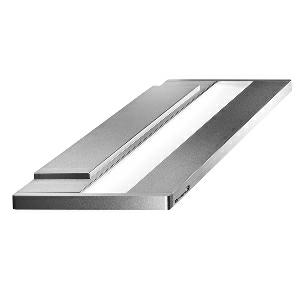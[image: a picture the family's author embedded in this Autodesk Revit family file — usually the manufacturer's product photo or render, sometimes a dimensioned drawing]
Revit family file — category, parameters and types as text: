
# Revit family: zera_bed_-_zew_11000_830_-_ul_nl_00813006_8f84
name_source: partatom
category: Lighting Fixtures
units: mm (PartAtom-declared; Revit-internal decimal feet)

## family parameters
Cut with Voids When Loaded = No
Host = Face
Light Source = No
Part Type = Normal
Room Calculation Point = No
Round Connector Dimension = Use Diameter
Shared = No

## types (1)
- AL+UL (1 x LED, 9800 lm, 4000K/3000K)
    Apparent Load = 109 VA
    Approval mark = CE
    CIE Flux Codes = 45 81 99 47 100
    Color Rendering = 90/80
    Color Temperature = 4000K/3000K
    Default Elevation = 2000 mm  [stored 6.56168 ft]
    Description = ZEW 11000/830|Wall-mounted luminaire|light source:   Warm white   |work equipment: Power supply unit|luminous flux: 10890 lm|light distribution: Direct/indirect|class of protection: I|technology: Switchable|mains lead: Connector 5 pin|glare control: Diffusor|special features: General light, indirect, 3000K, Ra80, DIN EN 60598-2-25, Reading light, direct, 2700K, Ra90, indir, dir 4K 60W Ra95|
    Frequency = 50 Hz, 60 Hz
    Height = 20 mm  [stored 0.0656168 ft]
    Lamp = 1 x LED
    Lamp Light Flux = 9800 lm
    Lamp count = 1
    Length = 1050 mm
    Luminous efficacy = 90 lm/W
    Manufacturer = Waldmann
    ModVariant = No
    Model = 00813006
    Mounting Place = Wall
    Mounting Type = Surface mounted
    Number of Poles = 1
    OnlyDefault = Yes
    Power Factor = 1
    Product Name = ZERA.bed - ZEW 11000/830 - UL/NL
    Product group = Wall mounted Luminaire
    ProductGroupID = 20
    Protection Class = Protection class I
    Protection Degree = IP 20
    RLX_Detail_Level = 1
    RLX_Emergency_Light_Flux = 0 lm
    RLX_Emergency_Type = 0
    RLX_Emergency_Type_DB = No
    RlxData = <blob elided: 60085 chars, md5=0de820ff>
    Socket = socket
    Standby Power = 0 W
    System Light Flux = 9800 lm
    System Power = 109 W
    Type Comments = General and Examation Light
    Type Image = zera_bed.jpg
    URL = http://relux.com
    VarID = al_ul_37f9
    Voltage = 230 V
    Voltage Range = 220-240 V
    Weight = 0.00 kg
    Width = 230 mm

note: [stored X ft] marks values corroborated as IEEE doubles in the binary element streams (Revit-internal decimal feet)

## geometry (parser evidence)
native form markers: Blend x4, Sweep x12
no freeform markers — native parametric forms only
